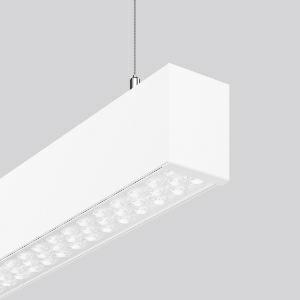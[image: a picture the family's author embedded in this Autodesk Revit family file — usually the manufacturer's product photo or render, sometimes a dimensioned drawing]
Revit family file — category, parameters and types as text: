
# Revit family: linedo_single_ip20_312564_002_1_7a37
name_source: partatom
category: Lighting Fixtures
units: mm (PartAtom-declared; Revit-internal decimal feet)

## family parameters
Cut with Voids When Loaded = No
Host = Face
Light Source = No
Part Type = Normal
Room Calculation Point = No
Round Connector Dimension = Use Diameter
Shared = No

## types (1)
- LINEDO single IP20 (1 x LED Modul 840, 6450 lm, 4000)
    Apparent Load = 40 VA
    CIE Flux Codes = 86 96 99 100 100
    Color Rendering = 80
    Color Temperature = 4000
    Default Elevation = 1800 mm
    Description = Series: LINEDO single IP20
Stylish pendant luminaire. Housing: extruded aluminium profile, powder-coated. End cap aluminium powder-coated, without visible screws. High-efficiency LED units with optimum light control thanks to clear plastic (PC) lens optics. 2-point steel cable suspension freely positionable and infinitely height-adjustable. With power cord (2.5 m). Please order canopy separately if required. Perfect for office areas (RUG < 19) and environments with computer screens in accordance with EN 12464-1. 
Colour: traffic white, matt (RAL 9016)
Length: 2264 mm
Width: 58 mm
Height: 76 mm
Suspension length: 100-1500 mm
Lamp: LED
Socket: without socket
Colour temperature: 4000K
Colour rendering index (CRI): 80
System power: 40 W
Rated luminous flux: 6450 lm
Beam angle Down: 59°
Luminous efficiency: 161 lm/W
Control gear: Regulated power supply
Protection class: I
Type of protection: IP 20
    Height = 76 mm
    Lamp = 1 x LED Modul 840
    Lamp Light Flux = 6450 lm
    Lamp count = 1
    Length = 2264 mm
    Lifetime = 50000 h
    Luminous efficacy = 161 lm/W
    Manufacturer = RZB
    ModVariant = No
    Model = 312564.002.1
    Mounting Place = Ceiling
    Mounting Type = Surface mounted, Pendant
    Number of Poles = 1
    OnlyDefault = Yes
    Power Factor = 1
    Product Name = LINEDO single IP20
    Product group = Pendant luminaires
    ProductGroupID = 902
    Protection Class = Protection class I
    Protection Degree = IP 20
    RLX_Detail_Level = 1
    RLX_Emergency_Light_Flux = 0 lm
    RLX_Emergency_Type = 0
    RLX_Emergency_Type_DB = No
    RlxData = <blob elided: 24333 chars, md5=f1c04e1f>
    Socket = socket
    Standby Power = 0 W
    System Light Flux = 6450 lm
    System Power = 40 W
    Type Comments = ALEA SPOT
    Type Image = 312563.002.jpg
    URL = http://relux.com
    VarID = ---
    Voltage = 230 V
    Voltage Range = 220-240 V
    Weight = 0.00 kg
    Width = 58 mm

## geometry (parser evidence)
native form markers: Blend x4, Sweep x11
no freeform markers — native parametric forms only
